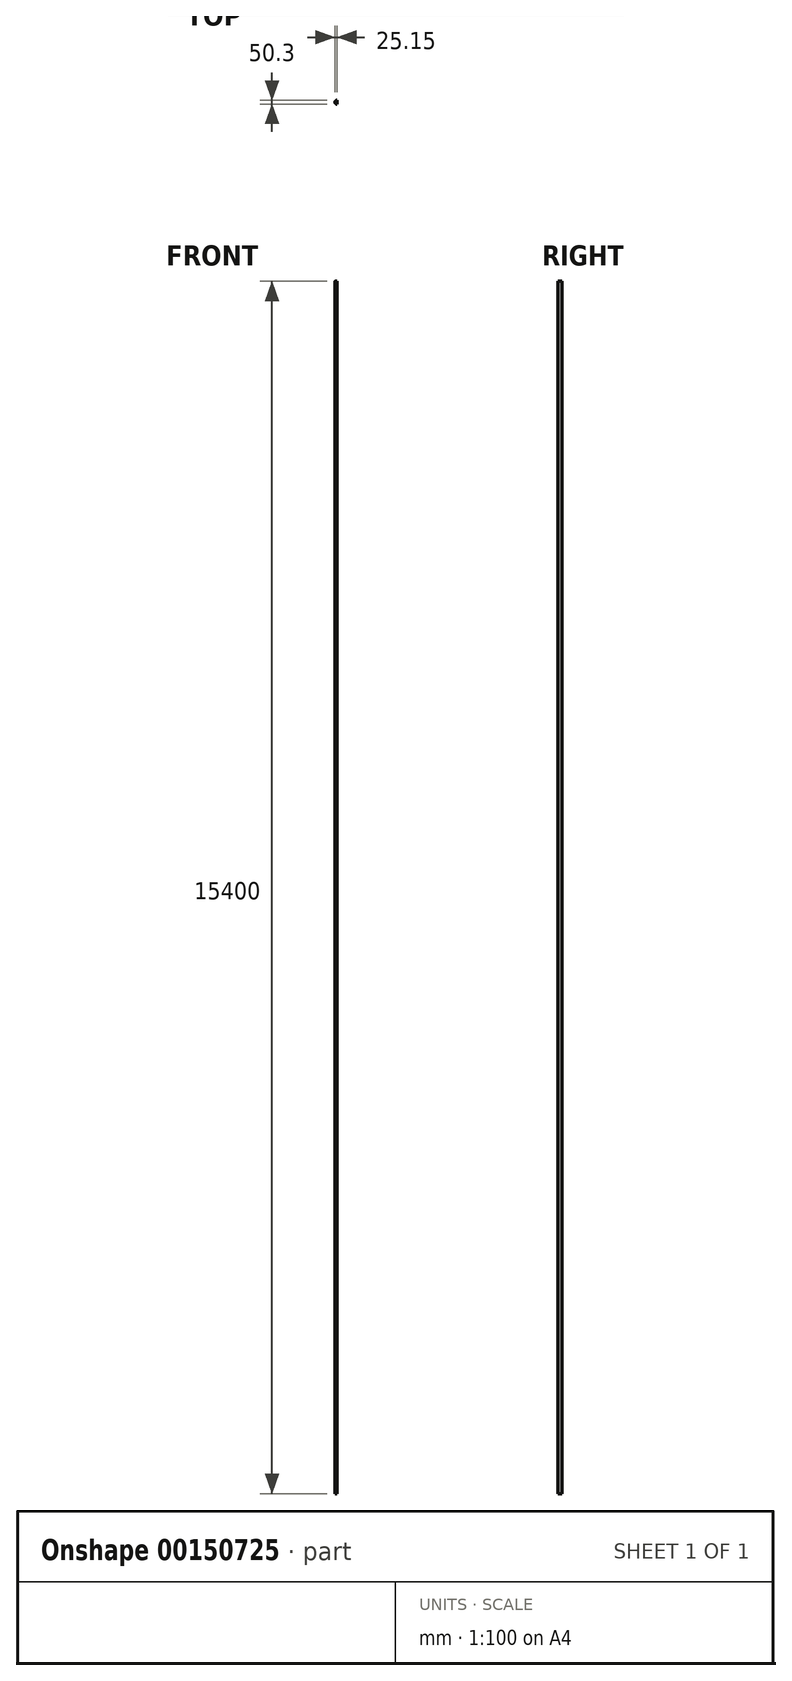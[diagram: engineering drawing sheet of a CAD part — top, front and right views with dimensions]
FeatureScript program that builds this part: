
annotation { "Feature Type Name" : "Feature", "Feature Type Description" : "" }
export const myFeature = defineFeature(function(context is Context, id is Id, definition is map)
    precondition{}
    {
        {
            var Q0;
            Q0=qCreatedBy(makeId("Front.planeOp"),FACE);
            var sketch = newSketch(context, id + "F0", { "sketchPlane" : qUnion([Q0])});
            skLineSegment(sketch, "E0.bottom", {"start": v(-25.15, 15400) * mm, "end": v(0, 15400) * mm});
            skLineSegment(sketch, "E0.top", {"start": v(-25.15, 0) * mm, "end": v(0, 0) * mm});
            skLineSegment(sketch, "E0.left", {"start": v(-25.15, 15400) * mm, "end": v(-25.15, 0) * mm});
            skLineSegment(sketch, "E0.right", {"start": v(0, 15400) * mm, "end": v(0, 0) * mm});
            skSolve(sketch);
        }
        {
            var Q0;
            Q0=makeQuery(id+"F0.imprint","IMPRINT",FACE,{"disambiguationData":[TD([[makeQuery(id+"F0.imprint","IMPRINT",EDGE,{"derivedFrom":sQuery(id+"F0.wireOp",EDGE,"E0.bottom")}),-1.0]])]});
            var Q1;
            Q1=sQuery(id+"F0.wireOp",EDGE,"E0.right");
            revolve(context, id + "F1", {"entities" : qUnion([Q0]), "axis" : qUnion([Q1]), "revolveType" : RevolveType.SYMMETRIC, "angle" : 180 * degree});
        }
    });
